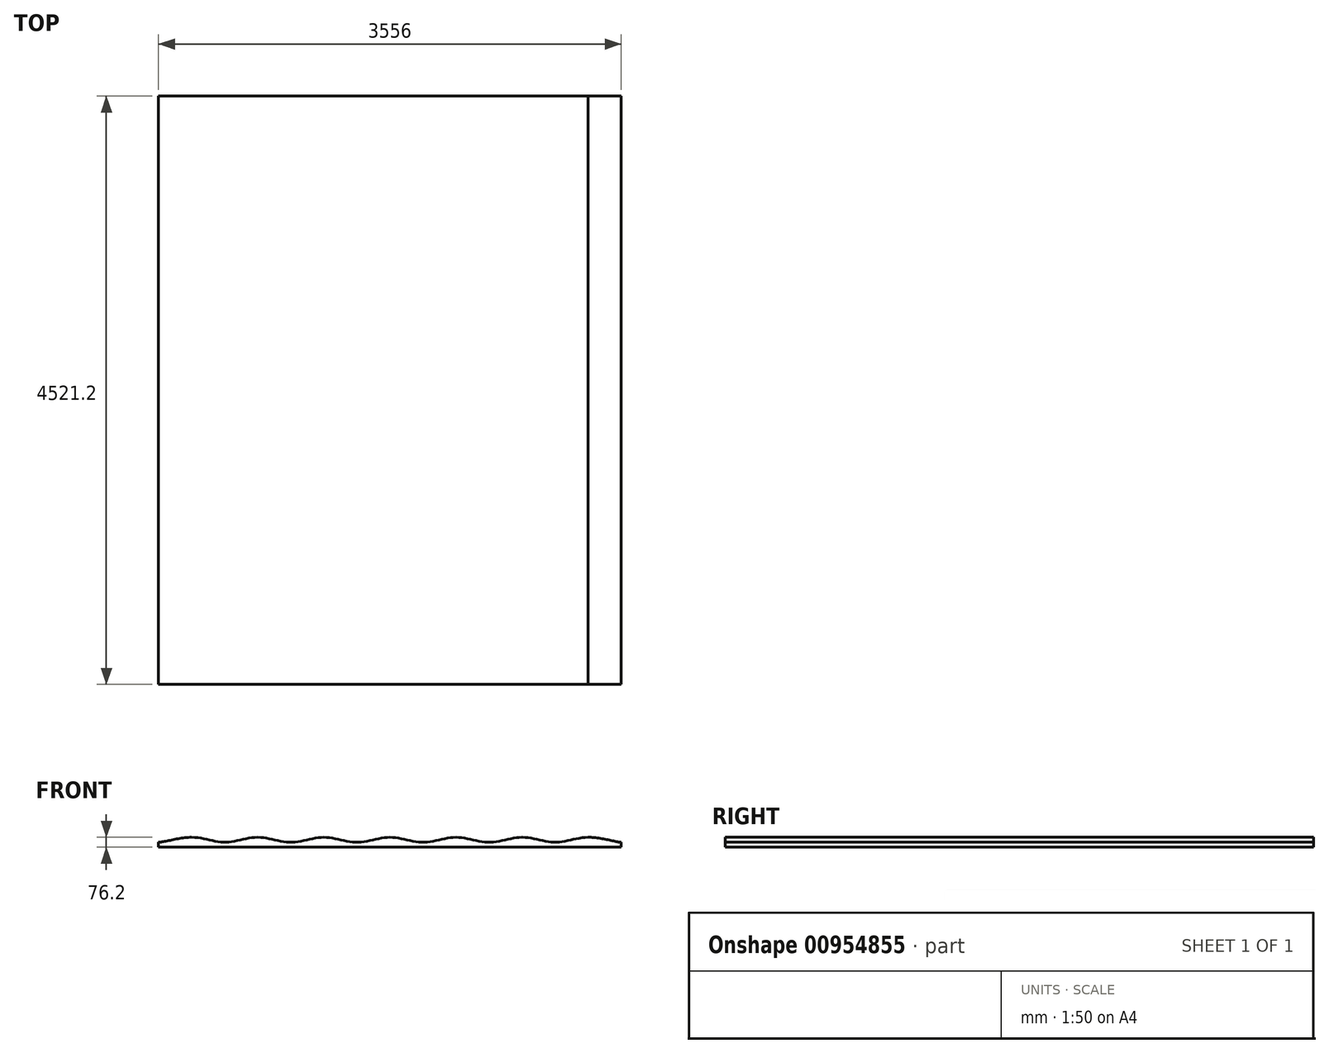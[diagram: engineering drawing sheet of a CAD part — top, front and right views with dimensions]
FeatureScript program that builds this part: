
annotation { "Feature Type Name" : "Feature", "Feature Type Description" : "" }
export const myFeature = defineFeature(function(context is Context, id is Id, definition is map)
    precondition{}
    {
        {
            var Q0;
            Q0=qCreatedBy(makeId("Front.planeOp"),FACE);
            var sketch = newSketch(context, id + "F0", { "sketchPlane" : qUnion([Q0])});
            skLineSegment(sketch, "E0.bottom", {"start": v(1778, 19.05) * mm, "end": v(-1778, 19.05) * mm, "construction": true});
            skLineSegment(sketch, "E0.top", {"start": v(1778, -19.05) * mm, "end": v(-1778, -19.05) * mm});
            skLineSegment(sketch, "E0.left", {"start": v(1778, 19.05) * mm, "end": v(1778, -19.05) * mm});
            skLineSegment(sketch, "E0.right", {"start": v(-1778, 19.05) * mm, "end": v(-1778, -19.05) * mm});
            skPoint(sketch, "E0.middle", {"position": v(0, 0) * mm});
            skLineSegment(sketch, "E1", {"start": v(-1778, 19.05) * mm, "end": v(-1524, 19.05) * mm, "construction": true});
            skLineSegment(sketch, "E2", {"start": v(-1524, 19.05) * mm, "end": v(-1270, 19.05) * mm, "construction": true});
            skLineSegment(sketch, "E3", {"start": v(-1270, 19.05) * mm, "end": v(-1016, 19.05) * mm, "construction": true});
            skLineSegment(sketch, "E4", {"start": v(-1016, 19.05) * mm, "end": v(-762, 19.05) * mm, "construction": true});
            skLineSegment(sketch, "E5", {"start": v(-762, 19.05) * mm, "end": v(-508, 19.05) * mm, "construction": true});
            skLineSegment(sketch, "E6", {"start": v(-508, 19.05) * mm, "end": v(-254, 19.05) * mm, "construction": true});
            skLineSegment(sketch, "E7", {"start": v(-254, 19.05) * mm, "end": v(0, 19.05) * mm, "construction": true});
            skLineSegment(sketch, "E8", {"start": v(0, 19.05) * mm, "end": v(254, 19.05) * mm, "construction": true});
            skLineSegment(sketch, "E9", {"start": v(254, 19.05) * mm, "end": v(508, 19.05) * mm, "construction": true});
            skLineSegment(sketch, "E10", {"start": v(508, 19.05) * mm, "end": v(762, 19.05) * mm, "construction": true});
            skLineSegment(sketch, "E11", {"start": v(762, 19.05) * mm, "end": v(1016, 19.05) * mm, "construction": true});
            skLineSegment(sketch, "E12", {"start": v(1016, 19.05) * mm, "end": v(1270, 19.05) * mm, "construction": true});
            skLineSegment(sketch, "E13", {"start": v(1270, 19.05) * mm, "end": v(1524, 19.05) * mm, "construction": true});
            skLineSegment(sketch, "E14", {"start": v(1524, 19.05) * mm, "end": v(1778, 19.05) * mm});
            skLineSegment(sketch, "E15", {"start": v(-1778, 19.05) * mm, "end": v(-1778, 57.15) * mm});
            skLineSegment(sketch, "E16", {"start": v(-1778, 57.15) * mm, "end": v(1778, 57.15) * mm});
            skPoint(sketch, "E17.9.internal.snap0", {"position": v(0, 57.15) * mm});
            skPoint(sketch, "E17.11.internal.snap0", {"position": v(0, 57.15) * mm});
            skPoint(sketch, "E17.13.internal.snap0", {"position": v(0, 57.15) * mm});
            skFitSpline(sketch, "E18", {"points": [v(-1778, 19.05) * mm, v(-1524, 57.15) * mm, v(-1270, 19.05) * mm, v(-1016, 57.15) * mm, v(-762, 19.05) * mm, v(-508, 57.15) * mm, v(-254, 19.05) * mm, v(0, 57.15) * mm, v(254, 19.05) * mm, v(508, 57.15) * mm, v(762, 19.05) * mm, v(1016, 57.15) * mm, v(1270, 19.05) * mm, v(1524, 57.15) * mm, v(1778, 19.05) * mm], "startDerivative": vector(1785.19, 0) * mm, "endDerivative": vector(2168.7, -149.12) * mm});
            skSolve(sketch);
        }
        {
            var Q0;
            Q0=makeQuery(id+"F0.imprint","IMPRINT",FACE,{"disambiguationData":[TD([[makeQuery(id+"F0.imprint","IMPRINT",EDGE,{"derivedFrom":sQuery(id+"F0.wireOp",EDGE,"E0.top")}),-1.0]])]});
            extrude(context, id + "F1", {"entities" : qUnion([Q0]), "depth" : 4521.2 * mm, "offsetDistance" : 25.4 * mm});
        }
    });
